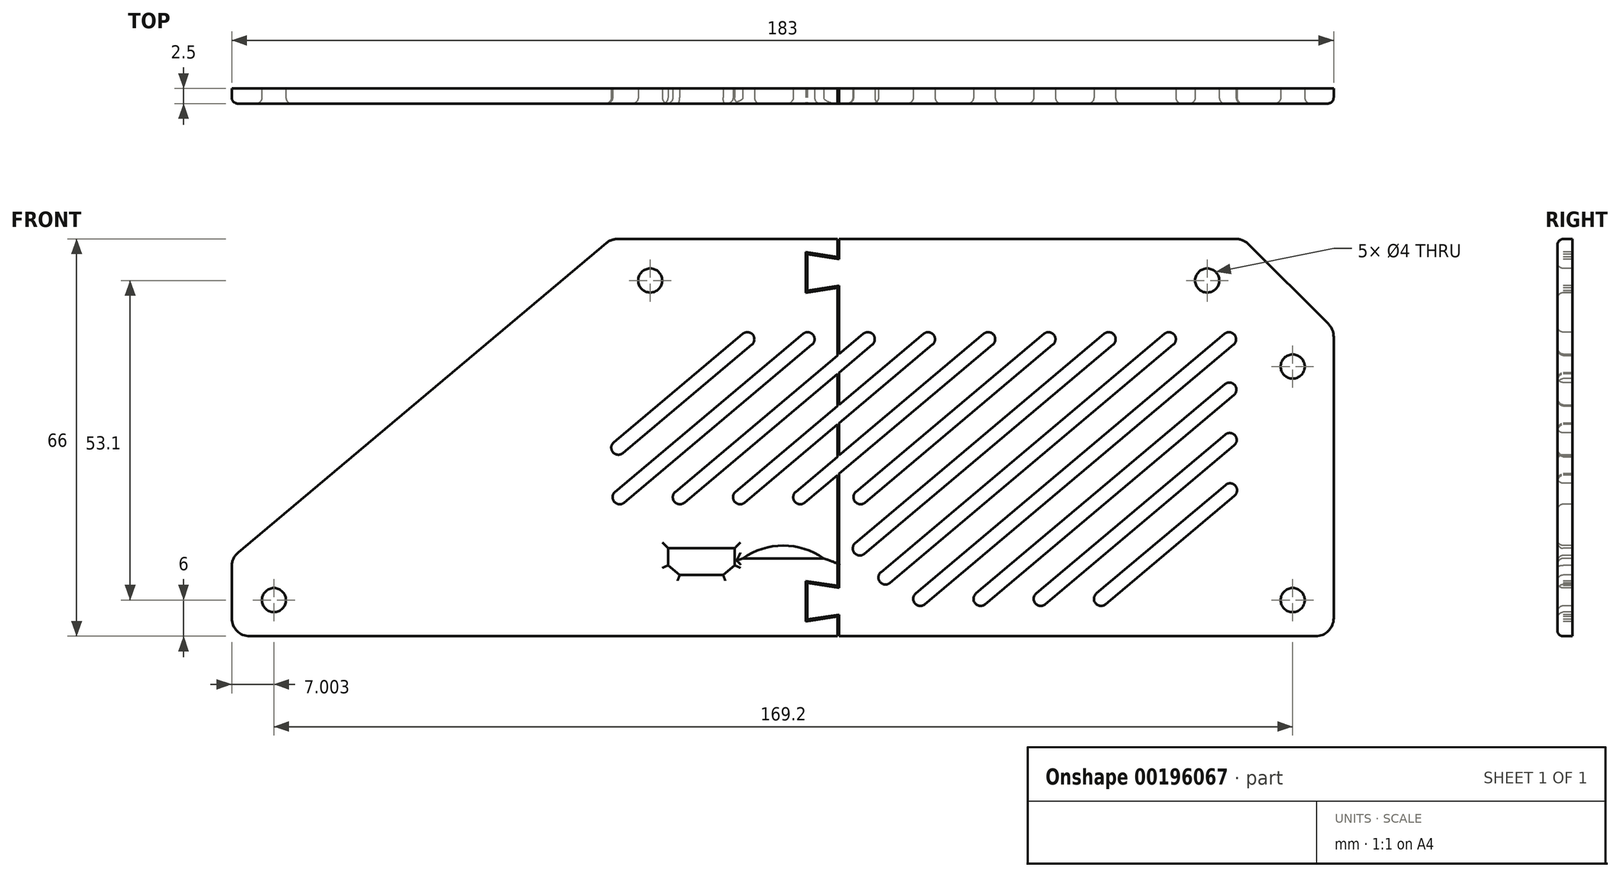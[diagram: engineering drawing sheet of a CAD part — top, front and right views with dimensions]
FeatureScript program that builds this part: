
annotation { "Feature Type Name" : "Feature", "Feature Type Description" : "" }
export const myFeature = defineFeature(function(context is Context, id is Id, definition is map)
    precondition{}
    {
        {
            var Q0;
            Q0=qCreatedBy(makeId("Front.planeOp"),FACE);
            var sketch = newSketch(context, id + "F0", { "sketchPlane" : qUnion([Q0])});
            skLineSegment(sketch, "E0.bottom", {"start": v(89.36, -33) * mm, "end": v(-93.64, -33) * mm});
            skLineSegment(sketch, "E0.top", {"start": v(89.36, 33) * mm, "end": v(-93.64, 33) * mm});
            skLineSegment(sketch, "E0.left", {"start": v(89.36, -33) * mm, "end": v(89.36, 33) * mm});
            skLineSegment(sketch, "E0.right", {"start": v(-93.64, -33) * mm, "end": v(-93.64, 33) * mm});
            skPoint(sketch, "E0.middle", {"position": v(-2.14, 0) * mm});
            skLineSegment(sketch, "E1", {"start": v(89.36, 18) * mm, "end": v(74.36, 33) * mm});
            skLineSegment(sketch, "E2", {"start": v(-93.64, -20) * mm, "end": v(-30.64, 33) * mm});
            skSolve(sketch);
        }
        {
            var Q0;
            {var subQ1=sQuery(id+"F0.wireOp",EDGE,"E0.bottom");Q0=makeQuery(id+"F0.imprint","IMPRINT",FACE,{"disambiguationData":[TD([[makeQuery(id+"F0.imprint","IMPRINT",EDGE,{"derivedFrom":subQ1}),-1.0]])]});}
            extrude(context, id + "F1", {"entities" : qUnion([Q0]), "depth" : 2.5 * mm});
        }
        {
            var Q0;
            Q0=makeQuery(id+"F1.opExtrude","CAP_FACE",FACE,{"disambiguationData":[OSD([sQuery(id+"F0.wireOp",EDGE,"E0.bottom"),sQuery(id+"F0.wireOp",EDGE,"E0.top"),sQuery(id+"F0.wireOp",EDGE,"E0.left"),sQuery(id+"F0.wireOp",EDGE,"E0.right"),sQuery(id+"F0.wireOp",EDGE,"E1"),sQuery(id+"F0.wireOp",EDGE,"E2")])],"isStart":false});
            var sketch = newSketch(context, id + "F2", { "sketchPlane" : qUnion([Q0])});
            skLineSegment(sketch, "E3", {"start": v(-24.14, 26.1) * mm, "end": v(68.36, 26.1) * mm});
            skLineSegment(sketch, "E4", {"start": v(82.56, 11.8) * mm, "end": v(82.56, -27) * mm});
            skLineSegment(sketch, "E5", {"start": v(82.56, -27) * mm, "end": v(-86.64, -27) * mm});
            skCircle(sketch, "E6", {"center": v(-24.14, 26.1) * mm, "radius": 2 * mm});
            skCircle(sketch, "E7", {"center": v(68.36, 26.1) * mm, "radius": 2 * mm});
            skCircle(sketch, "E8", {"center": v(82.56, 11.8) * mm, "radius": 2 * mm});
            skCircle(sketch, "E9", {"center": v(82.56, -27) * mm, "radius": 2 * mm});
            skCircle(sketch, "E10", {"center": v(-86.64, -27) * mm, "radius": 2 * mm});
            skLineSegment(sketch, "E11.bottom", {"start": v(4.66, -22.8) * mm, "end": v(-21.14, -22.8) * mm});
            skLineSegment(sketch, "E11.top", {"start": v(4.66, -17.7) * mm, "end": v(-21.14, -17.7) * mm});
            skLineSegment(sketch, "E11.left", {"start": v(4.66, -22.8) * mm, "end": v(4.66, -17.7) * mm});
            skLineSegment(sketch, "E11.right", {"start": v(-21.14, -22.8) * mm, "end": v(-21.14, -17.7) * mm});
            skPoint(sketch, "E11.middle", {"position": v(-8.24, -20.25) * mm});
            skLineSegment(sketch, "E12.bottom", {"start": v(4.66, -22.8) * mm, "end": v(-8.76, -22.8) * mm});
            skLineSegment(sketch, "E12.top", {"start": v(4.66, -20.08) * mm, "end": v(-8.76, -20.08) * mm});
            skLineSegment(sketch, "E12.left", {"start": v(4.66, -22.8) * mm, "end": v(4.66, -20.08) * mm});
            skLineSegment(sketch, "E12.right", {"start": v(-8.76, -22.8) * mm, "end": v(-8.76, -20.08) * mm});
            skArc(sketch, "E13", {"start": v(4.66, -20.08) * mm, "mid": v(-2.05, -17.94) * mm, "end": v(-8.76, -20.08) * mm});
            skLineSegment(sketch, "E14.bottom", {"start": v(-21.14, -22.8) * mm, "end": v(-10.14, -22.8) * mm});
            skLineSegment(sketch, "E14.top", {"start": v(-21.14, -18.4) * mm, "end": v(-10.14, -18.4) * mm});
            skLineSegment(sketch, "E14.left", {"start": v(-21.14, -22.8) * mm, "end": v(-21.14, -18.4) * mm});
            skLineSegment(sketch, "E14.right", {"start": v(-10.14, -22.8) * mm, "end": v(-10.14, -18.4) * mm});
            skLineSegment(sketch, "E15", {"start": v(-21.14, -21.2) * mm, "end": v(-19.24, -22.8) * mm});
            skLineSegment(sketch, "E16", {"start": v(-10.14, -21.2) * mm, "end": v(-12.04, -22.8) * mm});
            skSolve(sketch);
        }
        {
            var Q0;
            Q0=makeQuery(id+"F2.imprint","IMPRINT",FACE,{"disambiguationData":[TD([[makeQuery(id+"F2.imprint","IMPRINT",EDGE,{"derivedFrom":sQuery(id+"F2.wireOp",EDGE,"E6")}),1.0]])]});
            var Q1;
            Q1=makeQuery(id+"F2.imprint","IMPRINT",FACE,{"disambiguationData":[TD([[makeQuery(id+"F2.imprint","IMPRINT",EDGE,{"derivedFrom":sQuery(id+"F2.wireOp",EDGE,"E7")}),1.0]])]});
            var Q2;
            Q2=makeQuery(id+"F2.imprint","IMPRINT",FACE,{"disambiguationData":[TD([[makeQuery(id+"F2.imprint","IMPRINT",EDGE,{"derivedFrom":sQuery(id+"F2.wireOp",EDGE,"E8")}),1.0]])]});
            var Q3;
            Q3=makeQuery(id+"F2.imprint","IMPRINT",FACE,{"disambiguationData":[TD([[makeQuery(id+"F2.imprint","IMPRINT",EDGE,{"derivedFrom":sQuery(id+"F2.wireOp",EDGE,"E10")}),1.0]])]});
            var Q4;
            {var subQ0=sQuery(id+"F2.wireOp",EDGE,"E5");var subQ1=sQuery(id+"F2.wireOp",EDGE,"E4");var subQ2=makeQuery(id+"F2.imprint","INTERSECT",VERTEX,{"derivedFrom":[subQ1,subQ0]});Q4=makeQuery(id+"F2.imprint","IMPRINT",FACE,{"disambiguationData":[TD([[makeQuery(id+"F2.imprint","IMPRINT",EDGE,{"disambiguationData":[TD([[subQ2,1.0]])],"derivedFrom":subQ1}),-1.0]])]});}
            var Q5;
            {var subQ0=sQuery(id+"F2.wireOp",EDGE,"E5");var subQ1=sQuery(id+"F2.wireOp",EDGE,"E4");var subQ2=makeQuery(id+"F2.imprint","INTERSECT",VERTEX,{"derivedFrom":[subQ1,subQ0]});Q5=makeQuery(id+"F2.imprint","IMPRINT",FACE,{"disambiguationData":[TD([[makeQuery(id+"F2.imprint","IMPRINT",EDGE,{"disambiguationData":[TD([[subQ2,1.0]])],"derivedFrom":subQ1}),1.0]])]});}
            var Q6;
            Q6=makeQuery(id+"F2.imprint","IMPRINT",FACE,{"disambiguationData":[TD([[makeQuery(id+"F2.imprint","IMPRINT",EDGE,{"derivedFrom":sQuery(id+"F2.wireOp",EDGE,"E12.top")}),-1.0]])]});
            var Q7;
            Q7=makeQuery(id+"F2.imprint","IMPRINT",FACE,{"disambiguationData":[TD([[makeQuery(id+"F2.imprint","IMPRINT",EDGE,{"derivedFrom":sQuery(id+"F2.wireOp",EDGE,"E12.bottom")}),-1.0]])]});
            var Q8;
            {var subQ1=sQuery(id+"F2.wireOp",EDGE,"E14.top");Q8=makeQuery(id+"F2.imprint","IMPRINT",FACE,{"disambiguationData":[TD([[makeQuery(id+"F2.imprint","IMPRINT",EDGE,{"derivedFrom":subQ1}),-1.0]])]});}
            extrude(context, id + "F3", {"entities" : qUnion([Q0, Q1, Q2, Q3, Q4, Q5, Q6, Q7, Q8]), "operationType" : NewBodyOperationType.REMOVE, "endBound" : BoundingType.THROUGH_ALL, "oppositeDirection" : true, "depth" : 25 * mm});
        }
        {
            var Q0;
            Q0=makeQuery(id+"F1.opExtrude","CAP_FACE",FACE,{"disambiguationData":[OSD([sQuery(id+"F0.wireOp",EDGE,"E0.bottom"),sQuery(id+"F0.wireOp",EDGE,"E0.top"),sQuery(id+"F0.wireOp",EDGE,"E0.left"),sQuery(id+"F0.wireOp",EDGE,"E0.right"),sQuery(id+"F0.wireOp",EDGE,"E1"),sQuery(id+"F0.wireOp",EDGE,"E2")])],"isStart":false});
            var sketch = newSketch(context, id + "F4", { "sketchPlane" : qUnion([Q0])});
            skLineSegment(sketch, "E17", {"start": v(2.74, 15.45) * mm, "end": v(-28.46, -10.8) * mm});
            skLineSegment(sketch, "E18", {"start": v(-29.97, -9.02) * mm, "end": v(1.24, 17.24) * mm});
            skArc(sketch, "E19", {"start": v(2.74, 15.45) * mm, "mid": v(2.88, 17.1) * mm, "end": v(1.24, 17.24) * mm});
            skArc(sketch, "E20", {"start": v(-29.97, -9.02) * mm, "mid": v(-30.11, -10.66) * mm, "end": v(-28.46, -10.8) * mm});
            skLineSegment(sketch, "E21.1.0.0", {"start": v(-19.97, -9.02) * mm, "end": v(11.24, 17.24) * mm});
            skLineSegment(sketch, "E21.1.0.1", {"start": v(12.74, 15.45) * mm, "end": v(-18.46, -10.8) * mm});
            skArc(sketch, "E21.1.0.2", {"start": v(12.74, 15.45) * mm, "mid": v(12.88, 17.1) * mm, "end": v(11.24, 17.24) * mm});
            skArc(sketch, "E21.1.0.3", {"start": v(-19.97, -9.02) * mm, "mid": v(-20.11, -10.66) * mm, "end": v(-18.46, -10.8) * mm});
            skLineSegment(sketch, "E21.2.0.0", {"start": v(-9.97, -9.02) * mm, "end": v(21.24, 17.24) * mm});
            skLineSegment(sketch, "E21.2.0.1", {"start": v(22.74, 15.45) * mm, "end": v(-8.46, -10.8) * mm});
            skArc(sketch, "E21.2.0.2", {"start": v(22.74, 15.45) * mm, "mid": v(22.88, 17.1) * mm, "end": v(21.24, 17.24) * mm});
            skArc(sketch, "E21.2.0.3", {"start": v(-9.97, -9.02) * mm, "mid": v(-10.11, -10.66) * mm, "end": v(-8.46, -10.8) * mm});
            skLineSegment(sketch, "E21.3.0.0", {"start": v(0.03, -9.02) * mm, "end": v(31.24, 17.24) * mm});
            skLineSegment(sketch, "E21.3.0.1", {"start": v(32.74, 15.45) * mm, "end": v(1.54, -10.8) * mm});
            skArc(sketch, "E21.3.0.2", {"start": v(32.74, 15.45) * mm, "mid": v(32.88, 17.1) * mm, "end": v(31.24, 17.24) * mm});
            skArc(sketch, "E21.3.0.3", {"start": v(0.03, -9.02) * mm, "mid": v(-0.11, -10.66) * mm, "end": v(1.54, -10.8) * mm});
            skLineSegment(sketch, "E21.4.0.0", {"start": v(10.03, -9.02) * mm, "end": v(41.24, 17.24) * mm});
            skLineSegment(sketch, "E21.4.0.1", {"start": v(42.74, 15.45) * mm, "end": v(11.54, -10.8) * mm});
            skArc(sketch, "E21.4.0.2", {"start": v(42.74, 15.45) * mm, "mid": v(42.88, 17.1) * mm, "end": v(41.24, 17.24) * mm});
            skArc(sketch, "E21.4.0.3", {"start": v(10.03, -9.02) * mm, "mid": v(9.89, -10.66) * mm, "end": v(11.54, -10.8) * mm});
            skLineSegment(sketch, "E21.direction1", {"start": v(-28.46, -10.8) * mm, "end": v(-18.46, -10.8) * mm, "construction": true});
            skLineSegment(sketch, "E22.4.0.0", {"start": v(9.91, -17.53) * mm, "end": v(51.24, 17.24) * mm});
            skLineSegment(sketch, "E22.4.0.1", {"start": v(52.74, 15.45) * mm, "end": v(11.42, -19.32) * mm});
            skArc(sketch, "E22.4.0.3", {"start": v(9.91, -17.53) * mm, "mid": v(9.77, -19.17) * mm, "end": v(11.42, -19.32) * mm});
            skArc(sketch, "E23", {"start": v(52.74, 15.45) * mm, "mid": v(52.88, 17.1) * mm, "end": v(51.24, 17.24) * mm});
            skLineSegment(sketch, "E24.1.0.0", {"start": v(14.18, -22.36) * mm, "end": v(61.24, 17.24) * mm});
            skLineSegment(sketch, "E24.1.0.1", {"start": v(62.74, 15.45) * mm, "end": v(15.68, -24.14) * mm});
            skLineSegment(sketch, "E24.2.0.0", {"start": v(19.97, -25.9) * mm, "end": v(71.24, 17.24) * mm});
            skLineSegment(sketch, "E24.2.0.1", {"start": v(72.74, 15.45) * mm, "end": v(21.47, -27.69) * mm});
            skArc(sketch, "E24.2.0.2", {"start": v(19.97, -25.9) * mm, "mid": v(19.82, -27.54) * mm, "end": v(21.47, -27.69) * mm});
            skLineSegment(sketch, "E24.3.0.0", {"start": v(29.97, -25.9) * mm, "end": v(71.29, 8.87) * mm});
            skLineSegment(sketch, "E24.3.0.1", {"start": v(72.8, 7.08) * mm, "end": v(31.47, -27.69) * mm});
            skArc(sketch, "E24.3.0.2", {"start": v(29.97, -25.9) * mm, "mid": v(29.82, -27.54) * mm, "end": v(31.47, -27.69) * mm});
            skLineSegment(sketch, "E24.4.0.0", {"start": v(39.97, -25.9) * mm, "end": v(71.34, 0.5) * mm});
            skLineSegment(sketch, "E24.4.0.1", {"start": v(72.85, -1.3) * mm, "end": v(41.47, -27.69) * mm});
            skArc(sketch, "E24.4.0.2", {"start": v(39.97, -25.9) * mm, "mid": v(39.82, -27.54) * mm, "end": v(41.47, -27.69) * mm});
            skLineSegment(sketch, "E24.5.0.0", {"start": v(49.97, -25.9) * mm, "end": v(71.4, -7.87) * mm});
            skLineSegment(sketch, "E24.5.0.1", {"start": v(72.9, -9.66) * mm, "end": v(51.47, -27.69) * mm});
            skArc(sketch, "E24.5.0.2", {"start": v(49.97, -25.9) * mm, "mid": v(49.82, -27.54) * mm, "end": v(51.47, -27.69) * mm});
            skLineSegment(sketch, "E24.6.0.0", {"start": v(-30.19, -0.79) * mm, "end": v(-8.76, 17.24) * mm});
            skLineSegment(sketch, "E24.6.0.1", {"start": v(-7.26, 15.45) * mm, "end": v(-28.68, -2.58) * mm});
            skArc(sketch, "E24.6.0.2", {"start": v(-30.19, -0.79) * mm, "mid": v(-30.33, -2.44) * mm, "end": v(-28.68, -2.58) * mm});
            skArc(sketch, "E25", {"start": v(62.74, 15.45) * mm, "mid": v(62.88, 17.1) * mm, "end": v(61.24, 17.24) * mm});
            skArc(sketch, "E26", {"start": v(72.74, 15.45) * mm, "mid": v(72.88, 17.1) * mm, "end": v(71.24, 17.24) * mm});
            skArc(sketch, "E27", {"start": v(-7.26, 15.45) * mm, "mid": v(-7.12, 17.1) * mm, "end": v(-8.76, 17.24) * mm});
            skArc(sketch, "E28", {"start": v(72.8, 7.08) * mm, "mid": v(72.94, 8.73) * mm, "end": v(71.29, 8.87) * mm});
            skArc(sketch, "E29", {"start": v(72.85, -1.3) * mm, "mid": v(72.99, 0.36) * mm, "end": v(71.34, 0.5) * mm});
            skArc(sketch, "E30", {"start": v(72.9, -9.66) * mm, "mid": v(73.04, -8.01) * mm, "end": v(71.4, -7.87) * mm});
            skArc(sketch, "E31", {"start": v(14.18, -22.36) * mm, "mid": v(14.03, -24) * mm, "end": v(15.68, -24.14) * mm});
            skSolve(sketch);
        }
        {
            var Q0;
            Q0=makeQuery(id+"F4.imprint","IMPRINT",FACE,{"disambiguationData":[TD([[makeQuery(id+"F4.imprint","IMPRINT",EDGE,{"derivedFrom":sQuery(id+"F4.wireOp",EDGE,"E17")}),-1.0]])]});
            var Q1;
            Q1=makeQuery(id+"F4.imprint","IMPRINT",FACE,{"disambiguationData":[TD([[makeQuery(id+"F4.imprint","IMPRINT",EDGE,{"derivedFrom":sQuery(id+"F4.wireOp",EDGE,"E21.1.0.0")}),-1.0]])]});
            var Q2;
            Q2=makeQuery(id+"F4.imprint","IMPRINT",FACE,{"disambiguationData":[TD([[makeQuery(id+"F4.imprint","IMPRINT",EDGE,{"derivedFrom":sQuery(id+"F4.wireOp",EDGE,"E21.2.0.0")}),-1.0]])]});
            var Q3;
            Q3=makeQuery(id+"F4.imprint","IMPRINT",FACE,{"disambiguationData":[TD([[makeQuery(id+"F4.imprint","IMPRINT",EDGE,{"derivedFrom":sQuery(id+"F4.wireOp",EDGE,"E21.3.0.0")}),-1.0]])]});
            var Q4;
            Q4=makeQuery(id+"F4.imprint","IMPRINT",FACE,{"disambiguationData":[TD([[makeQuery(id+"F4.imprint","IMPRINT",EDGE,{"derivedFrom":sQuery(id+"F4.wireOp",EDGE,"E21.4.0.0")}),-1.0]])]});
            var Q5;
            Q5=makeQuery(id+"F4.imprint","IMPRINT",FACE,{"disambiguationData":[TD([[makeQuery(id+"F4.imprint","IMPRINT",EDGE,{"derivedFrom":sQuery(id+"F4.wireOp",EDGE,"E22.4.0.0")}),-1.0]])]});
            var Q6;
            Q6=makeQuery(id+"F4.imprint","IMPRINT",FACE,{"disambiguationData":[TD([[makeQuery(id+"F4.imprint","IMPRINT",EDGE,{"derivedFrom":sQuery(id+"F4.wireOp",EDGE,"E24.1.0.0")}),-1.0]])]});
            var Q7;
            Q7=makeQuery(id+"F4.imprint","IMPRINT",FACE,{"disambiguationData":[TD([[makeQuery(id+"F4.imprint","IMPRINT",EDGE,{"derivedFrom":sQuery(id+"F4.wireOp",EDGE,"E24.2.0.0")}),-1.0]])]});
            var Q8;
            Q8=makeQuery(id+"F4.imprint","IMPRINT",FACE,{"disambiguationData":[TD([[makeQuery(id+"F4.imprint","IMPRINT",EDGE,{"derivedFrom":sQuery(id+"F4.wireOp",EDGE,"E24.3.0.0")}),-1.0]])]});
            var Q9;
            Q9=makeQuery(id+"F4.imprint","IMPRINT",FACE,{"disambiguationData":[TD([[makeQuery(id+"F4.imprint","IMPRINT",EDGE,{"derivedFrom":sQuery(id+"F4.wireOp",EDGE,"E24.4.0.0")}),-1.0]])]});
            var Q10;
            Q10=makeQuery(id+"F4.imprint","IMPRINT",FACE,{"disambiguationData":[TD([[makeQuery(id+"F4.imprint","IMPRINT",EDGE,{"derivedFrom":sQuery(id+"F4.wireOp",EDGE,"E24.5.0.0")}),-1.0]])]});
            var Q11;
            Q11=makeQuery(id+"F4.imprint","IMPRINT",FACE,{"disambiguationData":[TD([[makeQuery(id+"F4.imprint","IMPRINT",EDGE,{"derivedFrom":sQuery(id+"F4.wireOp",EDGE,"E24.6.0.0")}),-1.0]])]});
            extrude(context, id + "F5", {"entities" : qUnion([Q0, Q1, Q2, Q3, Q4, Q5, Q6, Q7, Q8, Q9, Q10, Q11]), "operationType" : NewBodyOperationType.REMOVE, "endBound" : BoundingType.THROUGH_ALL, "oppositeDirection" : true, "depth" : 25 * mm});
        }
        {
            var Q0;
            Q0=makeQuery(id+"F1.opExtrude","CAP_FACE",FACE,{"disambiguationData":[OSD([sQuery(id+"F0.wireOp",EDGE,"E0.bottom"),sQuery(id+"F0.wireOp",EDGE,"E0.top"),sQuery(id+"F0.wireOp",EDGE,"E0.left"),sQuery(id+"F0.wireOp",EDGE,"E0.right"),sQuery(id+"F0.wireOp",EDGE,"E1"),sQuery(id+"F0.wireOp",EDGE,"E2")])],"isStart":false});
            var sketch = newSketch(context, id + "F6", { "sketchPlane" : qUnion([Q0])});
            skLineSegment(sketch, "E32", {"start": v(7.22, 33) * mm, "end": v(7.22, -33) * mm});
            skLineSegment(sketch, "E33", {"start": v(6.97, 33) * mm, "end": v(6.97, -33) * mm});
            skLineSegment(sketch, "E34", {"start": v(6.97, 27.44) * mm, "end": v(1.97, 27.44) * mm});
            skLineSegment(sketch, "E35", {"start": v(1.97, 27.44) * mm, "end": v(1.97, 30.46) * mm});
            skLineSegment(sketch, "E36", {"start": v(1.97, 30.46) * mm, "end": v(6.97, 29.7) * mm});
            skLineSegment(sketch, "E37.MirrorCS", {"start": v(1.97, 24.42) * mm, "end": v(6.97, 25.19) * mm});
            skLineSegment(sketch, "E38.MirrorCS", {"start": v(1.97, 27.44) * mm, "end": v(1.97, 24.42) * mm});
            skLineSegment(sketch, "E39", {"start": v(6.97, 30.02) * mm, "end": v(1.72, 30.83) * mm});
            skLineSegment(sketch, "E40", {"start": v(1.72, 30.83) * mm, "end": v(1.72, 27.44) * mm});
            skLineSegment(sketch, "E41.MirrorCS", {"start": v(6.97, 24.86) * mm, "end": v(1.72, 24.06) * mm});
            skLineSegment(sketch, "E42.MirrorCS", {"start": v(1.72, 24.06) * mm, "end": v(1.72, 27.44) * mm});
            skLineSegment(sketch, "E43.MirrorCS", {"start": v(6.97, -27.19) * mm, "end": v(1.97, -27.19) * mm});
            skLineSegment(sketch, "E44.MirrorCS", {"start": v(1.97, -30.21) * mm, "end": v(6.97, -29.44) * mm});
            skLineSegment(sketch, "E45.MirrorCS", {"start": v(6.97, -29.77) * mm, "end": v(1.72, -30.57) * mm});
            skLineSegment(sketch, "E46.MirrorCS", {"start": v(1.97, -27.19) * mm, "end": v(1.97, -30.21) * mm});
            skLineSegment(sketch, "E47.MirrorCS", {"start": v(1.72, -30.57) * mm, "end": v(1.72, -27.19) * mm});
            skLineSegment(sketch, "E48.MirrorCS", {"start": v(1.72, -23.8) * mm, "end": v(1.72, -27.19) * mm});
            skLineSegment(sketch, "E49.MirrorCS", {"start": v(1.97, -27.19) * mm, "end": v(1.97, -24.16) * mm});
            skLineSegment(sketch, "E50.MirrorCS", {"start": v(6.97, -24.6) * mm, "end": v(1.72, -23.8) * mm});
            skLineSegment(sketch, "E51.MirrorCS", {"start": v(1.97, -24.16) * mm, "end": v(6.97, -24.93) * mm});
            skLineSegment(sketch, "E52", {"start": v(6.97, -24.93) * mm, "end": v(7.22, -24.97) * mm});
            skLineSegment(sketch, "E53", {"start": v(6.97, -29.44) * mm, "end": v(7.22, -29.4) * mm});
            skLineSegment(sketch, "E54", {"start": v(6.97, 29.7) * mm, "end": v(7.22, 29.66) * mm});
            skLineSegment(sketch, "E55", {"start": v(6.97, 25.19) * mm, "end": v(7.22, 25.22) * mm});
            skSolve(sketch);
        }
        {
            var Q0;
            Q0=makeQuery(id+"F1.opExtrude","CAP_FACE",FACE,{"disambiguationData":[OSD([sQuery(id+"F0.wireOp",EDGE,"E0.bottom"),sQuery(id+"F0.wireOp",EDGE,"E0.top"),sQuery(id+"F0.wireOp",EDGE,"E0.left"),sQuery(id+"F0.wireOp",EDGE,"E0.right"),sQuery(id+"F0.wireOp",EDGE,"E1"),sQuery(id+"F0.wireOp",EDGE,"E2")])],"isStart":false});
            fillet(context, id + "F7", {"entities" : qUnion([Q0]), "radius" : 1 * mm, "tangentPropagation" : true, "allowEdgeOverflow" : false});
        }
        {
            var Q0;
            Q0=makeQuery(id+"F1.opExtrude","SWEPT_EDGE",EDGE,{"disambiguationData":[OSD([sQuery(id+"F0.wireOp",EDGE,"E0.bottom"),sQuery(id+"F0.wireOp",EDGE,"E0.right")])]});
            var Q1;
            Q1=makeQuery(id+"F1.opExtrude","SWEPT_EDGE",EDGE,{"disambiguationData":[OSD([sQuery(id+"F0.wireOp",EDGE,"E0.right"),sQuery(id+"F0.wireOp",EDGE,"E2")])]});
            var Q2;
            Q2=makeQuery(id+"F1.opExtrude","SWEPT_EDGE",EDGE,{"disambiguationData":[OSD([sQuery(id+"F0.wireOp",EDGE,"E0.top"),sQuery(id+"F0.wireOp",EDGE,"E2")])]});
            var Q3;
            Q3=makeQuery(id+"F1.opExtrude","SWEPT_EDGE",EDGE,{"disambiguationData":[OSD([sQuery(id+"F0.wireOp",EDGE,"E0.top"),sQuery(id+"F0.wireOp",EDGE,"E1")])]});
            var Q4;
            Q4=makeQuery(id+"F1.opExtrude","SWEPT_EDGE",EDGE,{"disambiguationData":[OSD([sQuery(id+"F0.wireOp",EDGE,"E0.left"),sQuery(id+"F0.wireOp",EDGE,"E1")])]});
            var Q5;
            Q5=makeQuery(id+"F1.opExtrude","SWEPT_EDGE",EDGE,{"disambiguationData":[OSD([sQuery(id+"F0.wireOp",EDGE,"E0.bottom"),sQuery(id+"F0.wireOp",EDGE,"E0.left")])]});
            fillet(context, id + "F8", {"entities" : qUnion([Q0, Q1, Q2, Q3, Q4, Q5]), "radius" : 3 * mm, "tangentPropagation" : true, "allowEdgeOverflow" : false});
        }
        {
            var Q0;
            Q0=makeQuery(id+"F6.imprint","IMPRINT",FACE,{"disambiguationData":[TD([[makeQuery(id+"F6.imprint","IMPRINT",EDGE,{"derivedFrom":sQuery(id+"F6.wireOp",EDGE,"E46.MirrorCS")}),-1.0]])]});
            var Q1;
            {var subQ0=sQuery(id+"F6.wireOp",EDGE,"E53");Q1=makeQuery(id+"F6.imprint","IMPRINT",FACE,{"disambiguationData":[TD([[makeQuery(id+"F6.imprint","IMPRINT",EDGE,{"derivedFrom":subQ0}),-1.0]])]});}
            var Q2;
            {var subQ0=sQuery(id+"F6.wireOp",EDGE,"E52");Q2=makeQuery(id+"F6.imprint","IMPRINT",FACE,{"disambiguationData":[TD([[makeQuery(id+"F6.imprint","IMPRINT",EDGE,{"derivedFrom":subQ0}),1.0]])]});}
            var Q3;
            {var subQ0=sQuery(id+"F6.wireOp",EDGE,"E32");var subQ1=makeQuery(id+"F5.boolean.opBoolean","COPY",EDGE,{"derivedFrom":makeQuery(id+"F5.opExtrude","CAP_EDGE",EDGE,{"disambiguationData":[OSD([sQuery(id+"F4.wireOp",EDGE,"E22.4.0.0")])],"isStart":true})});var subQ2=makeQuery(id+"F6.imprint","INTERSECT",VERTEX,{"derivedFrom":[subQ1,subQ0]});Q3=makeQuery(id+"F6.imprint","IMPRINT",FACE,{"disambiguationData":[TD([[makeQuery(id+"F6.imprint","IMPRINT",EDGE,{"disambiguationData":[TD([[subQ2,-1.0]])],"derivedFrom":subQ0}),-1.0]])]});}
            var Q4;
            {var subQ0=sQuery(id+"F6.wireOp",EDGE,"E32");var subQ1=makeQuery(id+"F5.boolean.opBoolean","COPY",EDGE,{"derivedFrom":makeQuery(id+"F5.opExtrude","CAP_EDGE",EDGE,{"disambiguationData":[OSD([sQuery(id+"F4.wireOp",EDGE,"E21.4.0.1")])],"isStart":true})});var subQ2=makeQuery(id+"F6.imprint","INTERSECT",VERTEX,{"derivedFrom":[subQ1,subQ0]});Q4=makeQuery(id+"F6.imprint","IMPRINT",FACE,{"disambiguationData":[TD([[makeQuery(id+"F6.imprint","IMPRINT",EDGE,{"disambiguationData":[TD([[subQ2,-1.0]])],"derivedFrom":subQ0}),-1.0]])]});}
            var Q5;
            {var subQ0=sQuery(id+"F6.wireOp",EDGE,"E32");var subQ1=makeQuery(id+"F5.boolean.opBoolean","COPY",EDGE,{"derivedFrom":makeQuery(id+"F5.opExtrude","CAP_EDGE",EDGE,{"disambiguationData":[OSD([sQuery(id+"F4.wireOp",EDGE,"E21.4.0.0")])],"isStart":true})});var subQ2=makeQuery(id+"F6.imprint","INTERSECT",VERTEX,{"derivedFrom":[subQ1,subQ0]});Q5=makeQuery(id+"F6.imprint","IMPRINT",FACE,{"disambiguationData":[TD([[makeQuery(id+"F6.imprint","IMPRINT",EDGE,{"disambiguationData":[TD([[subQ2,-1.0]])],"derivedFrom":subQ0}),-1.0]])]});}
            var Q6;
            {var subQ0=sQuery(id+"F6.wireOp",EDGE,"E32");var subQ1=makeQuery(id+"F5.boolean.opBoolean","COPY",EDGE,{"derivedFrom":makeQuery(id+"F5.opExtrude","CAP_EDGE",EDGE,{"disambiguationData":[OSD([sQuery(id+"F4.wireOp",EDGE,"E21.3.0.1")])],"isStart":true})});var subQ2=makeQuery(id+"F6.imprint","INTERSECT",VERTEX,{"derivedFrom":[subQ1,subQ0]});Q6=makeQuery(id+"F6.imprint","IMPRINT",FACE,{"disambiguationData":[TD([[makeQuery(id+"F6.imprint","IMPRINT",EDGE,{"disambiguationData":[TD([[subQ2,-1.0]])],"derivedFrom":subQ0}),-1.0]])]});}
            var Q7;
            {var subQ0=sQuery(id+"F6.wireOp",EDGE,"E32");var subQ1=makeQuery(id+"F5.boolean.opBoolean","COPY",EDGE,{"derivedFrom":makeQuery(id+"F5.opExtrude","CAP_EDGE",EDGE,{"disambiguationData":[OSD([sQuery(id+"F4.wireOp",EDGE,"E21.3.0.0")])],"isStart":true})});var subQ2=makeQuery(id+"F6.imprint","INTERSECT",VERTEX,{"derivedFrom":[subQ1,subQ0]});Q7=makeQuery(id+"F6.imprint","IMPRINT",FACE,{"disambiguationData":[TD([[makeQuery(id+"F6.imprint","IMPRINT",EDGE,{"disambiguationData":[TD([[subQ2,-1.0]])],"derivedFrom":subQ0}),-1.0]])]});}
            var Q8;
            {var subQ0=sQuery(id+"F6.wireOp",EDGE,"E32");var subQ1=makeQuery(id+"F5.boolean.opBoolean","COPY",EDGE,{"derivedFrom":makeQuery(id+"F5.opExtrude","CAP_EDGE",EDGE,{"disambiguationData":[OSD([sQuery(id+"F4.wireOp",EDGE,"E21.2.0.1")])],"isStart":true})});var subQ2=makeQuery(id+"F6.imprint","INTERSECT",VERTEX,{"derivedFrom":[subQ1,subQ0]});Q8=makeQuery(id+"F6.imprint","IMPRINT",FACE,{"disambiguationData":[TD([[makeQuery(id+"F6.imprint","IMPRINT",EDGE,{"disambiguationData":[TD([[subQ2,-1.0]])],"derivedFrom":subQ0}),-1.0]])]});}
            var Q9;
            {var subQ0=sQuery(id+"F6.wireOp",EDGE,"E32");var subQ1=makeQuery(id+"F5.boolean.opBoolean","COPY",EDGE,{"derivedFrom":makeQuery(id+"F5.opExtrude","CAP_EDGE",EDGE,{"disambiguationData":[OSD([sQuery(id+"F4.wireOp",EDGE,"E21.2.0.0")])],"isStart":true})});var subQ2=makeQuery(id+"F6.imprint","INTERSECT",VERTEX,{"derivedFrom":[subQ1,subQ0]});Q9=makeQuery(id+"F6.imprint","IMPRINT",FACE,{"disambiguationData":[TD([[makeQuery(id+"F6.imprint","IMPRINT",EDGE,{"disambiguationData":[TD([[subQ2,-1.0]])],"derivedFrom":subQ0}),-1.0]])]});}
            var Q10;
            {var subQ0=sQuery(id+"F6.wireOp",EDGE,"E32");var subQ1=makeQuery(id+"F5.boolean.opBoolean","COPY",EDGE,{"derivedFrom":makeQuery(id+"F5.opExtrude","CAP_EDGE",EDGE,{"disambiguationData":[OSD([sQuery(id+"F4.wireOp",EDGE,"E21.1.0.1")])],"isStart":true})});var subQ2=makeQuery(id+"F6.imprint","INTERSECT",VERTEX,{"derivedFrom":[subQ1,subQ0]});Q10=makeQuery(id+"F6.imprint","IMPRINT",FACE,{"disambiguationData":[TD([[makeQuery(id+"F6.imprint","IMPRINT",EDGE,{"disambiguationData":[TD([[subQ2,-1.0]])],"derivedFrom":subQ0}),-1.0]])]});}
            var Q11;
            {var subQ0=sQuery(id+"F6.wireOp",EDGE,"E32");var subQ1=makeQuery(id+"F5.boolean.opBoolean","COPY",EDGE,{"derivedFrom":makeQuery(id+"F5.opExtrude","CAP_EDGE",EDGE,{"disambiguationData":[OSD([sQuery(id+"F4.wireOp",EDGE,"E21.1.0.2")])],"isStart":true})});var subQ2=makeQuery(id+"F6.imprint","INTERSECT",VERTEX,{"derivedFrom":[subQ1,subQ0]});Q11=makeQuery(id+"F6.imprint","IMPRINT",FACE,{"disambiguationData":[TD([[makeQuery(id+"F6.imprint","IMPRINT",EDGE,{"disambiguationData":[TD([[subQ2,-1.0]])],"derivedFrom":subQ0}),-1.0]])]});}
            var Q12;
            {var subQ0=sQuery(id+"F6.wireOp",EDGE,"E55");Q12=makeQuery(id+"F6.imprint","IMPRINT",FACE,{"disambiguationData":[TD([[makeQuery(id+"F6.imprint","IMPRINT",EDGE,{"derivedFrom":subQ0}),-1.0]])]});}
            var Q13;
            Q13=makeQuery(id+"F6.imprint","IMPRINT",FACE,{"disambiguationData":[TD([[makeQuery(id+"F6.imprint","IMPRINT",EDGE,{"derivedFrom":sQuery(id+"F6.wireOp",EDGE,"E35")}),1.0]])]});
            var Q14;
            {var subQ0=sQuery(id+"F6.wireOp",EDGE,"E54");Q14=makeQuery(id+"F6.imprint","IMPRINT",FACE,{"disambiguationData":[TD([[makeQuery(id+"F6.imprint","IMPRINT",EDGE,{"derivedFrom":subQ0}),1.0]])]});}
            extrude(context, id + "F9", {"entities" : qUnion([Q0, Q1, Q2, Q3, Q4, Q5, Q6, Q7, Q8, Q9, Q10, Q11, Q12, Q13, Q14]), "operationType" : NewBodyOperationType.REMOVE, "endBound" : BoundingType.THROUGH_ALL, "oppositeDirection" : true, "depth" : 25 * mm});
        }
    });
